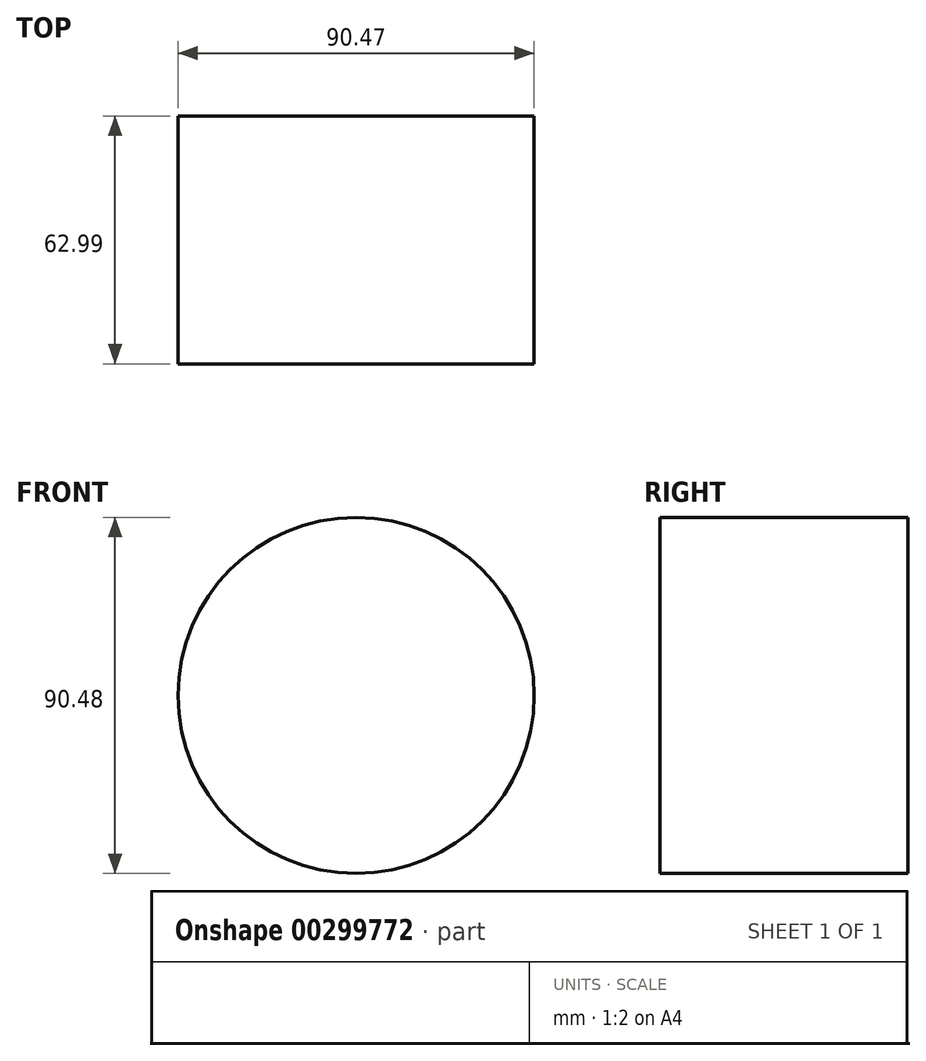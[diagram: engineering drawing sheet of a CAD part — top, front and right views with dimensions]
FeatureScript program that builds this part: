
annotation { "Feature Type Name" : "Feature", "Feature Type Description" : "" }
export const myFeature = defineFeature(function(context is Context, id is Id, definition is map)
    precondition{}
    {
        {
            var Q0;
            Q0=qCreatedBy(makeId("Front.planeOp"),FACE);
            var sketch = newSketch(context, id + "F0", { "sketchPlane" : qUnion([Q0])});
            skCircle(sketch, "E0", {"center": v(-2.33, 0) * mm, "radius": 45.24 * mm});
            skSolve(sketch);
        }
        {
            var Q0;
            Q0=makeQuery(id+"F0.imprint","IMPRINT",FACE,{"disambiguationData":[TD([[makeQuery(id+"F0.imprint","IMPRINT",EDGE,{"derivedFrom":sQuery(id+"F0.wireOp",EDGE,"E0")}),1.0]])]});
            var sketch = newSketch(context, id + "F1", { "sketchPlane" : qUnion([Q0])});
            skSolve(sketch);
        }
        {
            var Q0;
            Q0=makeQuery(id+"F1.imprint","IMPRINT",FACE,{"disambiguationData":[TD([[makeQuery(id+"F1.imprint","IMPRINT",EDGE,{"derivedFrom":makeQuery(id+"F0.imprint","IMPRINT",EDGE,{"derivedFrom":sQuery(id+"F0.wireOp",EDGE,"E0")})}),1.0]])]});
            var Q1;
            Q1=makeQuery(id+"F0.imprint","IMPRINT",FACE,{"disambiguationData":[TD([[makeQuery(id+"F0.imprint","IMPRINT",EDGE,{"derivedFrom":sQuery(id+"F0.wireOp",EDGE,"E0")}),1.0]])]});
            extrude(context, id + "F2", {"entities" : qUnion([Q0, Q1]), "depth" : 63 * mm});
        }
    });
